# Revit family: KS Polar plus, DS 40, Ø168,3-323,9
name_source: partatom
category: HLS-Bauteile
revit_build: Autodesk Revit 2018 (Build: 20190510_1515(x64)
units: mm (PartAtom-declared; Revit-internal decimal feet)

## family parameters
Arbeitsebenenbasiert = Ja
Beim Laden mit Abzugskörper schneiden = Nein
Bemaßung runder Anschluss = Durchmesser verwenden
Gemeinsam genutzt = Ja
Immer vertikal = Nein
Raumberechnungspunkt = Nein
Teiletyp = Normal

## types (4) — shared parameters
A = 60 mm
Anschluss = M16
Baustoffklasse = B2
DF2 = 20 mm  [stored 0.0656168 ft]
DS = 40 mm  [stored 0.131234 ft]
DVS = 13 mm
Dichte Kern = 145 kg/m³
Dämmkörper = AC/PU
Dämmstärke = 40 mm  [stored 0.131234 ft]
Fabrikat = MEFA
Firma = MEFA Befestigungs- und Montagesysteme GmbH
HGA = 15 mm  [stored 0.0492126 ft]
Kurztext1 = Kälteschelle Polar Plus
L = 66 mm  [stored 0.216535 ft]
MB = 50 mm  [stored 0.164042 ft]
MD = 5 mm  [stored 0.0164042 ft]
Material = Stahl
Materialname = S235
Mengeneinheit = St
Oberflaeche = galvanisch verzinkt
Rohrschellentyp = Titan HD
Schalenlänge = 66 mm
Vorgabe-Ansicht = 1219 mm
Wasserdampfdiffusionswiderstand = 7000 µ
Wärmeleitfähigkeit = 0.031 W/mK
max. Temperaturbeständigkeit = 105 °C
mittl. Nenndruckfestigkeit Kern = 1,9 N/mm²
stat. Belastung Kern = 0,38 N/mm²
vpe = 1 St
zero-valued in all types: AB

## per-type parameters (varying)
| type | Anschlußhöhe | Artikelnummer | B | Breite | D | D0 | DF1 | EAN | Gewicht | Gewicht pro Bauteil | H | Kurztext2 | R | RM | Rohraußendurchmesser Stahl | S | max. zul. Last |
| Kälteschelle Polar plus, DS 40, M16, Ø168,3 | 56 mm | 746416802 | 333 mm | 330 mm | 168 mm | 248 mm | 22 mm | 4250928442956 | 2.23 kg | 2.23 kg | 273 mm | 168,3 mm Iso 40 x 66 mm M16 | 124 mm | 129 mm | 168,3 mm | 311 mm | 4.02 kN |
| Kälteschelle Polar plus, DS 40, M16, Ø219,1 | 55 mm | 746421903 | 384 mm | 380 mm | 219 mm | 299 mm | 22 mm | 4250928442963 | 2.60 kg | 2.60 kg | 324 mm | 219,1 mm Iso 40 x 66 mm M16 | 150 mm | 155 mm | 219,1 mm | 362 mm | 5.23 kN |
| Kälteschelle Polar plus, DS 40, M16, Ø273 | 56 mm | 746427302 | 438 mm  [stored 1.43701 ft] | 428 mm | 273 mm | 353 mm  [stored 1.15814 ft] | 22 mm | 4250928442970 | 3.03 kg | 3.03 kg | 378 mm | 273 mm Iso 40 x 66 mm M16 | 177 mm | 182 mm | 273 mm | 416 mm  [stored 1.36483 ft] | 6.52 kN |
| Kälteschelle Polar plus, DS 40, M16, Ø323,9 | 56 mm | 746432404 | 488 mm | 486 mm | 324 mm | 404 mm | 21 mm | 4250928442987 | 3.41 kg | 3.41 kg | 429 mm | 323,9 mm Iso 40 x 66 mm M16 | 202 mm | 207 mm | 323,9 mm | 467 mm | 7.73 kN |

note: [stored X ft] marks values corroborated as IEEE doubles in the binary element streams (Revit-internal decimal feet)

## geometry (parser evidence)
native form markers: Sweep x2
no freeform markers — native parametric forms only
